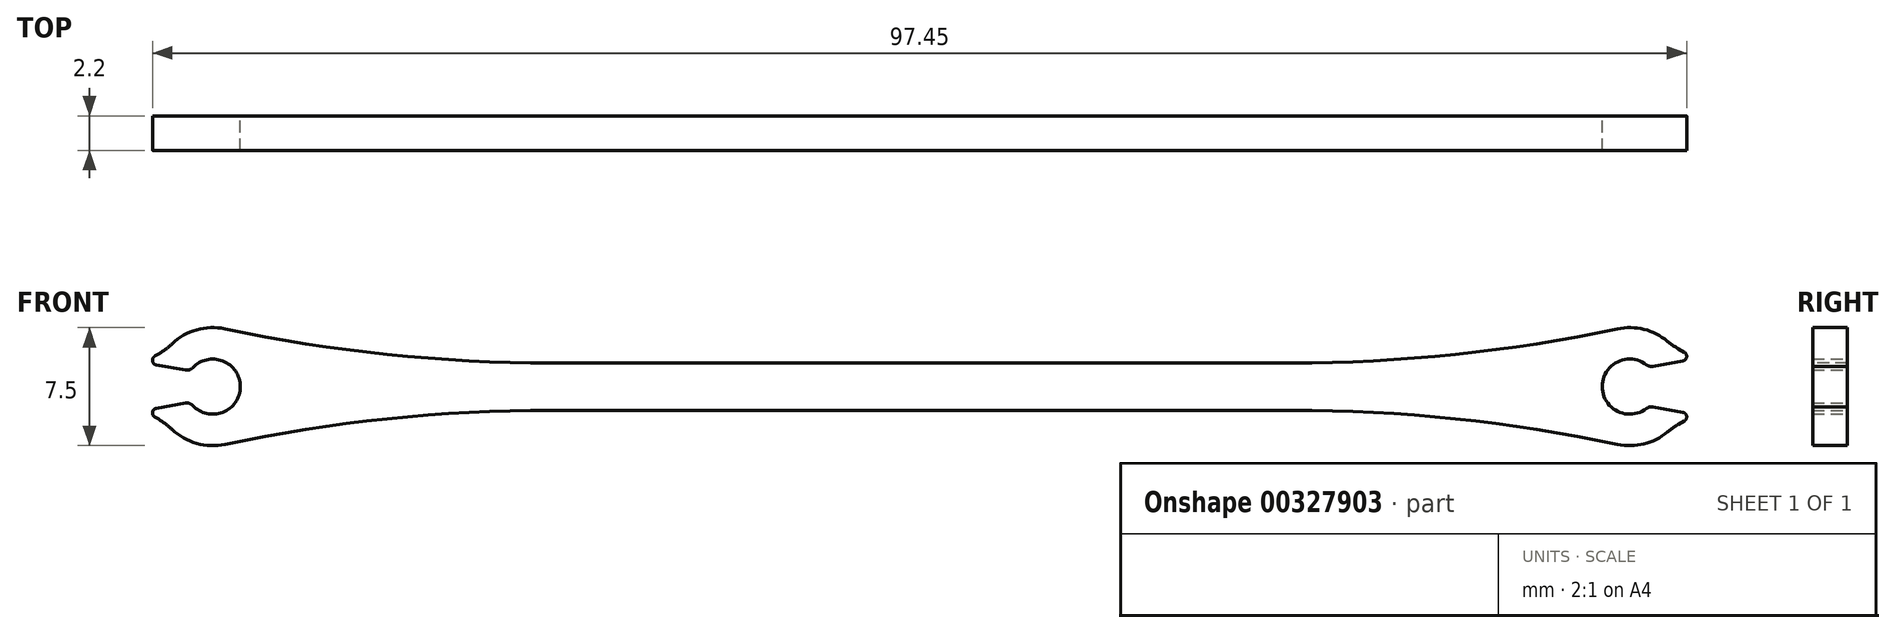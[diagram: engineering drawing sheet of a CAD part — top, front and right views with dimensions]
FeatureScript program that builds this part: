
annotation { "Feature Type Name" : "Feature", "Feature Type Description" : "" }
export const myFeature = defineFeature(function(context is Context, id is Id, definition is map)
    precondition{}
    {
        {
            var Q0;
            Q0=qCreatedBy(makeId("Front.planeOp"),FACE);
            var sketch = newSketch(context, id + "F0", { "sketchPlane" : qUnion([Q0])});
            skArc(sketch, "E0", {"start": v(1.22, 1.25) * mm, "mid": v(-1.75, 0) * mm, "end": v(1.22, -1.25) * mm});
            skArc(sketch, "E1", {"start": v(2.65, 2.65) * mm, "mid": v(-0.7, 3.68) * mm, "end": v(-3.44, 1.5) * mm});
            skLineSegment(sketch, "E2", {"start": v(-3.44, 1.5) * mm, "end": v(-86.56, 1.5) * mm});
            skLineSegment(sketch, "E3", {"start": v(-3.44, -1.5) * mm, "end": v(-86.56, -1.5) * mm});
            skArc(sketch, "E4.trimOffspring", {"start": v(-3.44, -1.5) * mm, "mid": v(-0.7, -3.68) * mm, "end": v(2.65, -2.65) * mm});
            skLineSegment(sketch, "E5", {"start": v(1.22, 1.25) * mm, "end": v(4.18, 1.77) * mm});
            skLineSegment(sketch, "E6", {"start": v(1.22, -1.25) * mm, "end": v(4.18, -1.77) * mm});
            skLineSegment(sketch, "E7", {"start": v(2.65, 2.65) * mm, "end": v(4.18, 1.77) * mm});
            skLineSegment(sketch, "E8", {"start": v(4.18, -1.77) * mm, "end": v(2.65, -2.65) * mm});
            skArc(sketch, "E9", {"start": v(-86.56, 1.5) * mm, "mid": v(-89.48, 3.71) * mm, "end": v(-92.9, 2.39) * mm});
            skArc(sketch, "E10", {"start": v(-91.44, -1) * mm, "mid": v(-88.25, 0) * mm, "end": v(-91.44, 1) * mm});
            skLineSegment(sketch, "E11", {"start": v(-91.44, -1) * mm, "end": v(-94.4, -1.52) * mm});
            skLineSegment(sketch, "E12", {"start": v(-91.44, 1) * mm, "end": v(-94.4, 1.52) * mm});
            skLineSegment(sketch, "E13", {"start": v(-94.4, 1.52) * mm, "end": v(-92.9, 2.39) * mm});
            skLineSegment(sketch, "E14", {"start": v(-94.4, -1.52) * mm, "end": v(-92.9, -2.39) * mm});
            skArc(sketch, "E15.trimOffspring", {"start": v(-92.9, -2.39) * mm, "mid": v(-89.48, -3.71) * mm, "end": v(-86.56, -1.5) * mm});
            skSolve(sketch);
        }
        {
            var Q0;
            Q0=makeQuery(id+"F0.imprint","IMPRINT",FACE,{"disambiguationData":[TD([[makeQuery(id+"F0.imprint","IMPRINT",EDGE,{"derivedFrom":sQuery(id+"F0.wireOp",EDGE,"E0")}),-1.0]])]});
            extrude(context, id + "F1", {"entities" : qUnion([Q0]), "endBound" : BoundingType.SYMMETRIC, "depth" : 2.2 * mm});
        }
        {
            var Q0;
            Q0=makeQuery(id+"F1.opExtrude","SWEPT_EDGE",EDGE,{"disambiguationData":[OSD([sQuery(id+"F0.wireOp",EDGE,"E5"),sQuery(id+"F0.wireOp",EDGE,"E7")])]});
            var Q1;
            Q1=makeQuery(id+"F1.opExtrude","SWEPT_EDGE",EDGE,{"disambiguationData":[OSD([sQuery(id+"F0.wireOp",EDGE,"E6"),sQuery(id+"F0.wireOp",EDGE,"E8")])]});
            var Q2;
            Q2=makeQuery(id+"F1.opExtrude","SWEPT_EDGE",EDGE,{"disambiguationData":[OSD([sQuery(id+"F0.wireOp",EDGE,"E11"),sQuery(id+"F0.wireOp",EDGE,"E14")])]});
            var Q3;
            Q3=makeQuery(id+"F1.opExtrude","SWEPT_EDGE",EDGE,{"disambiguationData":[OSD([sQuery(id+"F0.wireOp",EDGE,"E12"),sQuery(id+"F0.wireOp",EDGE,"E13")])]});
            fillet(context, id + "F2", {"entities" : qUnion([Q0, Q1, Q2, Q3]), "radius" : 0.3 * mm, "tangentPropagation" : true, "allowEdgeOverflow" : false});
        }
        {
            var Q0;
            Q0=makeQuery(id+"F1.opExtrude","SWEPT_EDGE",EDGE,{"disambiguationData":[OSD([sQuery(id+"F0.wireOp",EDGE,"E1"),sQuery(id+"F0.wireOp",EDGE,"E2")])]});
            var Q1;
            Q1=makeQuery(id+"F1.opExtrude","SWEPT_EDGE",EDGE,{"disambiguationData":[OSD([sQuery(id+"F0.wireOp",EDGE,"E3"),sQuery(id+"F0.wireOp",EDGE,"E4.trimOffspring")])]});
            var Q2;
            Q2=makeQuery(id+"F1.opExtrude","SWEPT_EDGE",EDGE,{"disambiguationData":[OSD([sQuery(id+"F0.wireOp",EDGE,"E2"),sQuery(id+"F0.wireOp",EDGE,"E9")])]});
            var Q3;
            Q3=makeQuery(id+"F1.opExtrude","SWEPT_EDGE",EDGE,{"disambiguationData":[OSD([sQuery(id+"F0.wireOp",EDGE,"E3"),sQuery(id+"F0.wireOp",EDGE,"E15.trimOffspring")])]});
            fillet(context, id + "F3", {"entities" : qUnion([Q0, Q1, Q2, Q3]), "radius" : 100 * mm, "tangentPropagation" : true, "allowEdgeOverflow" : false});
        }
        {
            var Q0;
            Q0=makeQuery(id+"F1.opExtrude","SWEPT_EDGE",EDGE,{"disambiguationData":[OSD([sQuery(id+"F0.wireOp",EDGE,"E0"),sQuery(id+"F0.wireOp",EDGE,"E5")])]});
            var Q1;
            Q1=makeQuery(id+"F1.opExtrude","SWEPT_EDGE",EDGE,{"disambiguationData":[OSD([sQuery(id+"F0.wireOp",EDGE,"E0"),sQuery(id+"F0.wireOp",EDGE,"E6")])]});
            var Q2;
            Q2=makeQuery(id+"F1.opExtrude","SWEPT_EDGE",EDGE,{"disambiguationData":[OSD([sQuery(id+"F0.wireOp",EDGE,"E10"),sQuery(id+"F0.wireOp",EDGE,"E12")])]});
            var Q3;
            Q3=makeQuery(id+"F1.opExtrude","SWEPT_EDGE",EDGE,{"disambiguationData":[OSD([sQuery(id+"F0.wireOp",EDGE,"E10"),sQuery(id+"F0.wireOp",EDGE,"E11")])]});
            fillet(context, id + "F4", {"entities" : qUnion([Q0, Q1, Q2, Q3]), "radius" : 0.5 * mm, "tangentPropagation" : true, "allowEdgeOverflow" : false});
        }
        {
            var Q0;
            Q0=makeQuery(id+"F1.opExtrude","SWEPT_EDGE",EDGE,{"disambiguationData":[OSD([sQuery(id+"F0.wireOp",EDGE,"E1"),sQuery(id+"F0.wireOp",EDGE,"E7")])]});
            var Q1;
            Q1=makeQuery(id+"F1.opExtrude","SWEPT_EDGE",EDGE,{"disambiguationData":[OSD([sQuery(id+"F0.wireOp",EDGE,"E4.trimOffspring"),sQuery(id+"F0.wireOp",EDGE,"E8")])]});
            var Q2;
            Q2=makeQuery(id+"F1.opExtrude","SWEPT_EDGE",EDGE,{"disambiguationData":[OSD([sQuery(id+"F0.wireOp",EDGE,"E14"),sQuery(id+"F0.wireOp",EDGE,"E15.trimOffspring")])]});
            var Q3;
            Q3=makeQuery(id+"F1.opExtrude","SWEPT_EDGE",EDGE,{"disambiguationData":[OSD([sQuery(id+"F0.wireOp",EDGE,"E9"),sQuery(id+"F0.wireOp",EDGE,"E13")])]});
            fillet(context, id + "F5", {"entities" : qUnion([Q0, Q1, Q2, Q3]), "radius" : 5 * mm, "tangentPropagation" : true, "allowEdgeOverflow" : false});
        }
    });
